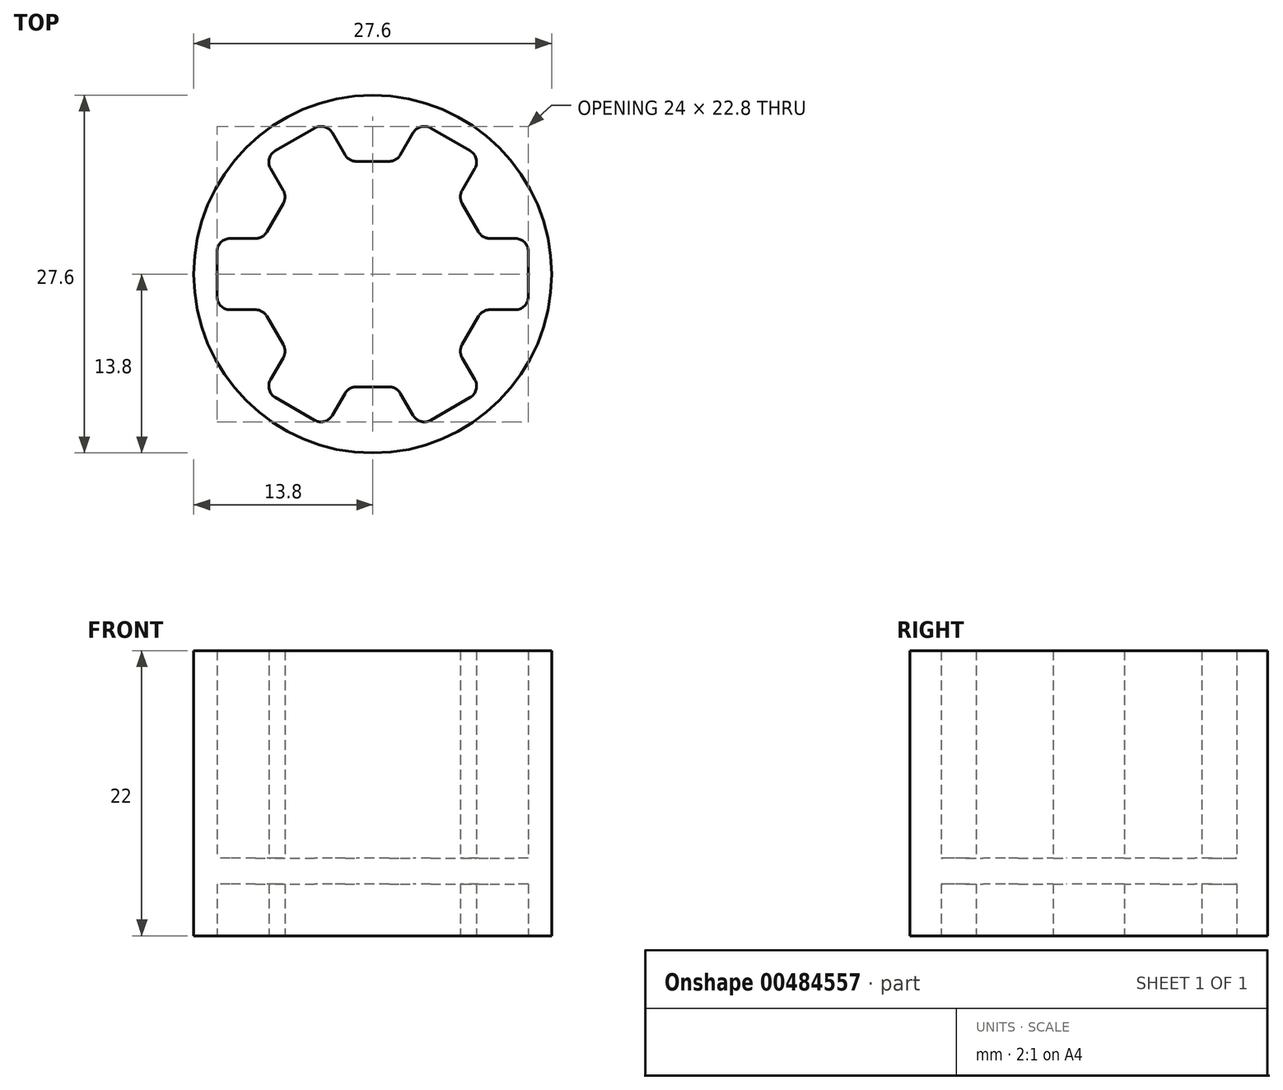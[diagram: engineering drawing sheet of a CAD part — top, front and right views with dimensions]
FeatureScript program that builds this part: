
annotation { "Feature Type Name" : "Feature", "Feature Type Description" : "" }
export const myFeature = defineFeature(function(context is Context, id is Id, definition is map)
    precondition{}
    {
        {
            var Q0;
            Q0=qCreatedBy(makeId("Top.planeOp"),FACE);
            var sketch = newSketch(context, id + "F0", { "sketchPlane" : qUnion([Q0])});
            skLineSegment(sketch, "E0", {"start": v(0, 8.7) * mm, "end": v(1.27, 8.7) * mm});
            skLineSegment(sketch, "E1", {"start": v(2.14, 9.2) * mm, "end": v(3.12, 10.9) * mm});
            skArc(sketch, "E2.filletArc", {"start": v(1.27, 8.7) * mm, "mid": v(1.77, 8.83) * mm, "end": v(2.14, 9.2) * mm});
            skLineSegment(sketch, "E3", {"start": v(4.48, 11.27) * mm, "end": v(6, 10.4) * mm});
            skLineSegment(sketch, "E4", {"start": v(0, 0) * mm, "end": v(6, 10.4) * mm, "construction": true});
            skArc(sketch, "E5", {"start": v(4.48, 11.27) * mm, "mid": v(3.73, 11.37) * mm, "end": v(3.12, 10.9) * mm});
            skPoint(sketch, "E6.center", {"position": v(0, 0) * mm});
            skArc(sketch, "E7.MirrorCS", {"start": v(6.9, 5.45) * mm, "mid": v(6.77, 5.95) * mm, "end": v(6.9, 6.45) * mm});
            skLineSegment(sketch, "E8.MirrorCS", {"start": v(7.52, 9.52) * mm, "end": v(6, 10.4) * mm});
            skLineSegment(sketch, "E9.MirrorCS", {"start": v(7.53, 4.35) * mm, "end": v(6.9, 5.45) * mm});
            skLineSegment(sketch, "E10.MirrorCS", {"start": v(6.9, 6.45) * mm, "end": v(7.88, 8.15) * mm});
            skArc(sketch, "E11.MirrorCS", {"start": v(7.52, 9.52) * mm, "mid": v(7.98, 8.91) * mm, "end": v(7.88, 8.15) * mm});
            skLineSegment(sketch, "E12.1.0", {"start": v(-2.14, 9.2) * mm, "end": v(-3.12, 10.9) * mm});
            skLineSegment(sketch, "E12.1.1", {"start": v(-7.52, 9.52) * mm, "end": v(-6, 10.4) * mm});
            skLineSegment(sketch, "E12.1.2", {"start": v(0, 8.7) * mm, "end": v(-1.27, 8.7) * mm});
            skArc(sketch, "E12.1.3", {"start": v(-7.52, 9.52) * mm, "mid": v(-7.98, 8.91) * mm, "end": v(-7.88, 8.15) * mm});
            skLineSegment(sketch, "E12.1.4", {"start": v(-4.48, 11.27) * mm, "end": v(-6, 10.4) * mm});
            skLineSegment(sketch, "E12.1.5", {"start": v(-6.9, 6.45) * mm, "end": v(-7.88, 8.15) * mm});
            skArc(sketch, "E12.1.6", {"start": v(-4.48, 11.27) * mm, "mid": v(-3.73, 11.37) * mm, "end": v(-3.12, 10.9) * mm});
            skLineSegment(sketch, "E12.1.7", {"start": v(-7.53, 4.35) * mm, "end": v(-6.9, 5.45) * mm});
            skArc(sketch, "E12.1.8", {"start": v(-1.27, 8.7) * mm, "mid": v(-1.77, 8.83) * mm, "end": v(-2.14, 9.2) * mm});
            skArc(sketch, "E12.1.9", {"start": v(-6.9, 5.45) * mm, "mid": v(-6.77, 5.95) * mm, "end": v(-6.9, 6.45) * mm});
            skLineSegment(sketch, "E12.2.0", {"start": v(-9.04, 2.75) * mm, "end": v(-11, 2.75) * mm});
            skLineSegment(sketch, "E12.2.1", {"start": v(-12, -1.75) * mm, "end": v(-12, 0) * mm});
            skLineSegment(sketch, "E12.2.2", {"start": v(-7.53, 4.35) * mm, "end": v(-8.17, 3.25) * mm});
            skArc(sketch, "E12.2.3", {"start": v(-12, -1.75) * mm, "mid": v(-11.7, -2.46) * mm, "end": v(-11, -2.75) * mm});
            skLineSegment(sketch, "E12.2.4", {"start": v(-12, 1.75) * mm, "end": v(-12, 0) * mm});
            skLineSegment(sketch, "E12.2.5", {"start": v(-9.04, -2.75) * mm, "end": v(-11, -2.75) * mm});
            skArc(sketch, "E12.2.6", {"start": v(-12, 1.75) * mm, "mid": v(-11.7, 2.46) * mm, "end": v(-11, 2.75) * mm});
            skLineSegment(sketch, "E12.2.7", {"start": v(-7.53, -4.35) * mm, "end": v(-8.17, -3.25) * mm});
            skArc(sketch, "E12.2.8", {"start": v(-8.17, 3.25) * mm, "mid": v(-8.54, 2.88) * mm, "end": v(-9.04, 2.75) * mm});
            skArc(sketch, "E12.2.9", {"start": v(-8.17, -3.25) * mm, "mid": v(-8.54, -2.88) * mm, "end": v(-9.04, -2.75) * mm});
            skLineSegment(sketch, "E12.3.0", {"start": v(-6.9, -6.45) * mm, "end": v(-7.88, -8.15) * mm});
            skLineSegment(sketch, "E12.3.1", {"start": v(-4.48, -11.27) * mm, "end": v(-6, -10.4) * mm});
            skLineSegment(sketch, "E12.3.2", {"start": v(-7.53, -4.35) * mm, "end": v(-6.9, -5.45) * mm});
            skArc(sketch, "E12.3.3", {"start": v(-4.48, -11.27) * mm, "mid": v(-3.73, -11.37) * mm, "end": v(-3.12, -10.9) * mm});
            skLineSegment(sketch, "E12.3.4", {"start": v(-7.52, -9.52) * mm, "end": v(-6, -10.4) * mm});
            skLineSegment(sketch, "E12.3.5", {"start": v(-2.14, -9.2) * mm, "end": v(-3.12, -10.9) * mm});
            skArc(sketch, "E12.3.6", {"start": v(-7.52, -9.52) * mm, "mid": v(-7.98, -8.91) * mm, "end": v(-7.88, -8.15) * mm});
            skLineSegment(sketch, "E12.3.7", {"start": v(0, -8.7) * mm, "end": v(-1.27, -8.7) * mm});
            skArc(sketch, "E12.3.8", {"start": v(-6.9, -5.45) * mm, "mid": v(-6.77, -5.95) * mm, "end": v(-6.9, -6.45) * mm});
            skArc(sketch, "E12.3.9", {"start": v(-1.27, -8.7) * mm, "mid": v(-1.77, -8.83) * mm, "end": v(-2.14, -9.2) * mm});
            skLineSegment(sketch, "E12.4.0", {"start": v(2.14, -9.2) * mm, "end": v(3.12, -10.9) * mm});
            skLineSegment(sketch, "E12.4.1", {"start": v(7.52, -9.52) * mm, "end": v(6, -10.4) * mm});
            skLineSegment(sketch, "E12.4.2", {"start": v(0, -8.7) * mm, "end": v(1.27, -8.7) * mm});
            skArc(sketch, "E12.4.3", {"start": v(7.52, -9.52) * mm, "mid": v(7.98, -8.91) * mm, "end": v(7.88, -8.15) * mm});
            skLineSegment(sketch, "E12.4.4", {"start": v(4.48, -11.27) * mm, "end": v(6, -10.4) * mm});
            skLineSegment(sketch, "E12.4.5", {"start": v(6.9, -6.45) * mm, "end": v(7.88, -8.15) * mm});
            skArc(sketch, "E12.4.6", {"start": v(4.48, -11.27) * mm, "mid": v(3.73, -11.37) * mm, "end": v(3.12, -10.9) * mm});
            skLineSegment(sketch, "E12.4.7", {"start": v(7.53, -4.35) * mm, "end": v(6.9, -5.45) * mm});
            skArc(sketch, "E12.4.8", {"start": v(1.27, -8.7) * mm, "mid": v(1.77, -8.83) * mm, "end": v(2.14, -9.2) * mm});
            skArc(sketch, "E12.4.9", {"start": v(6.9, -5.45) * mm, "mid": v(6.77, -5.95) * mm, "end": v(6.9, -6.45) * mm});
            skLineSegment(sketch, "E12.5.0", {"start": v(9.04, -2.75) * mm, "end": v(11, -2.75) * mm});
            skLineSegment(sketch, "E12.5.1", {"start": v(12, 1.75) * mm, "end": v(12, 0) * mm});
            skLineSegment(sketch, "E12.5.2", {"start": v(7.53, -4.35) * mm, "end": v(8.17, -3.25) * mm});
            skArc(sketch, "E12.5.3", {"start": v(12, 1.75) * mm, "mid": v(11.7, 2.46) * mm, "end": v(11, 2.75) * mm});
            skLineSegment(sketch, "E12.5.4", {"start": v(12, -1.75) * mm, "end": v(12, 0) * mm});
            skLineSegment(sketch, "E12.5.5", {"start": v(9.04, 2.75) * mm, "end": v(11, 2.75) * mm});
            skArc(sketch, "E12.5.6", {"start": v(12, -1.75) * mm, "mid": v(11.7, -2.46) * mm, "end": v(11, -2.75) * mm});
            skLineSegment(sketch, "E12.5.7", {"start": v(7.53, 4.35) * mm, "end": v(8.17, 3.25) * mm});
            skArc(sketch, "E12.5.8", {"start": v(8.17, -3.25) * mm, "mid": v(8.54, -2.88) * mm, "end": v(9.04, -2.75) * mm});
            skArc(sketch, "E12.5.9", {"start": v(8.17, 3.25) * mm, "mid": v(8.54, 2.88) * mm, "end": v(9.04, 2.75) * mm});
            skCircle(sketch, "E13", {"center": v(0, 0) * mm, "radius": 13.8 * mm});
            skSolve(sketch);
        }
        {
            var Q0;
            Q0=makeQuery(id+"F0.imprint","IMPRINT",FACE,{"disambiguationData":[TD([[makeQuery(id+"F0.imprint","IMPRINT",EDGE,{"derivedFrom":sQuery(id+"F0.wireOp",EDGE,"E0")}),1.0]])]});
            extrude(context, id + "F1", {"entities" : qUnion([Q0]), "depth" : 16 * mm, "hasSecondDirection" : true, "secondDirectionOppositeDirection" : true, "secondDirectionDepth" : 6 * mm, "offsetDistance" : 25 * mm});
        }
        {
            var Q0;
            Q0=qCreatedBy(makeId("Top.planeOp"),FACE);
            var sketch = newSketch(context, id + "F2", { "sketchPlane" : qUnion([Q0])});
            skCircle(sketch, "E14", {"center": v(0, 0) * mm, "radius": 13.8 * mm});
            skSolve(sketch);
        }
        {
            var Q0;
            Q0 = qSketchRegion(id + "F2", true);
            extrude(context, id + "F3", {"entities" : qUnion([Q0]), "operationType" : NewBodyOperationType.ADD, "oppositeDirection" : true, "depth" : 2 * mm, "offsetDistance" : 25 * mm});
        }
    });
